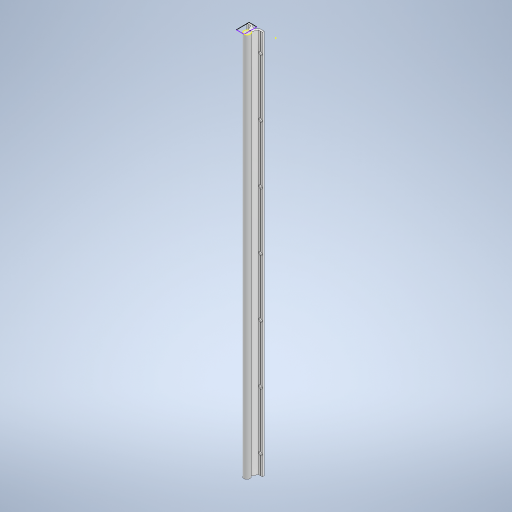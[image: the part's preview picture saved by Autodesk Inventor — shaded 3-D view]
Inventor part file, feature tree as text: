
AUTODESK INVENTOR PART (.ipt)
format: ipt  version: 2024 (Build 280153000, 153)  size: 6,572,544 bytes
history: native  units: in
note: dims shown in document units (in); Inventor stores cm internally (conversion verified against a paired STEP export)
features: other x9, sketch x1
ambient origin geometry x8: Origin, YZ Plane, XZ Plane, XY Plane, X Axis, Y Axis, Z Axis, Center Point
bodies: Solid1 (feature_tree), Solid2 (feature_tree), Solid3 (feature_tree), Solid4 (feature_tree), Solid5 (feature_tree), Solid6 (feature_tree), Solid7 (feature_tree), Solid8 (feature_tree), Solid9 (feature_tree)
feature tree (10):
  sketch  "Sketch1"
  other  "Guide 16mm"
  other  "Rail"
  other  "M5x20mm DIN912"
  other  "M5x20mm DIN912:1"
  other  "M5x20mm DIN912:2"
  other  "M5x20mm DIN912:3"
  other  "M5x20mm DIN912:4"
  other  "M5x20mm DIN912:5"
  other  "M5x20mm DIN912:6"
